# Revit family: Dual_Hands-free_Activation_Bi-level_ADA_Cooler-Elkay-LZOOSTL8LC
name_source: partatom
category: Plumbing Fixtures
units: mm (PartAtom-declared; Revit-internal decimal feet)

## family parameters
Always vertical = Yes
Cut with Voids When Loaded = No
Maintain Annotation Orientation = No
OmniClass Number = 23.65.70.14.11
OmniClass Title = Drinking Fountains/Coolers
Part Type = Normal
Room Calculation Point = No
Round Connector Dimension = Use Diameter
Shared = No
Work Plane-Based = No

## types (1)
- LZOOSTL8LC  (Dual Hands-free Activation Wall Mount Bi-level ADA Cooler)
    Activation Method = Electronic Sensor Bubbler
    Approx. Shipping Weight (lbs) = 74
    Assembly Code = D2010.60
    CW Connection = No
    Chilling Capacity(GPH) = 8
    Connector Outlet B = 1.5 "
    Connector Supply A = 0.375 "
    Current = 0 A
    Default Elevation = 0 "
    Description = Dual Hands-free Activation Bi-level ADA Cooler Filtered Refrigerated Light Gray
    Dimensions (L x W x H) = "36 3/4 inch x 19 inch x 25 5/16 inch"
    Electrical connection distance from center = 0 "
    Inlet Connection Size (inch) = 0.375 "
    Installation Location = Indoor
    Main Material = Finish-Elkay-Steel
    Manufacturer = Elkay Manufacturer Company
    Manufacturer Brand = Elkay (by Zurn Elkay Water Solutions)
    Masking A1 = 21.444 "
    Masking A2 = 21.01 "
    Masking Arc Radius = 21 "
    Material_Shroud = Finish-Elkay-Light Gray
    Material_Wrapper = Finish-Elkay-Light Gray(1)
    Model = LZOOSTL8LC
    Mounting Type = Wall Mount (On Wall)
    Number of Poles = 1
    Outlet Connection Size (inch) = 1.5
    Power Factor = 1
    Product Documentation Link = https://www.elkayfiles.com
    Product Installation Sheet URL = https://www.elkayfiles.com
    Product Page URL = https://www.elkay.com
    Product Weight (lbs) = 63
    Product data URL = https://bimobject.com
    Repair Parts URL = https://www.elkayfiles.com
    Right Hand Version = Yes
    Right Hand Version_Fine Detail = Yes
    Right Hand masking region = Yes
    URL = https://www.elkay.com
    Voltage = 115 V
    Waste Connection = No
    sensor button = 0 "

## geometry (parser evidence)
native form markers: Sweep x22
no freeform markers — native parametric forms only
